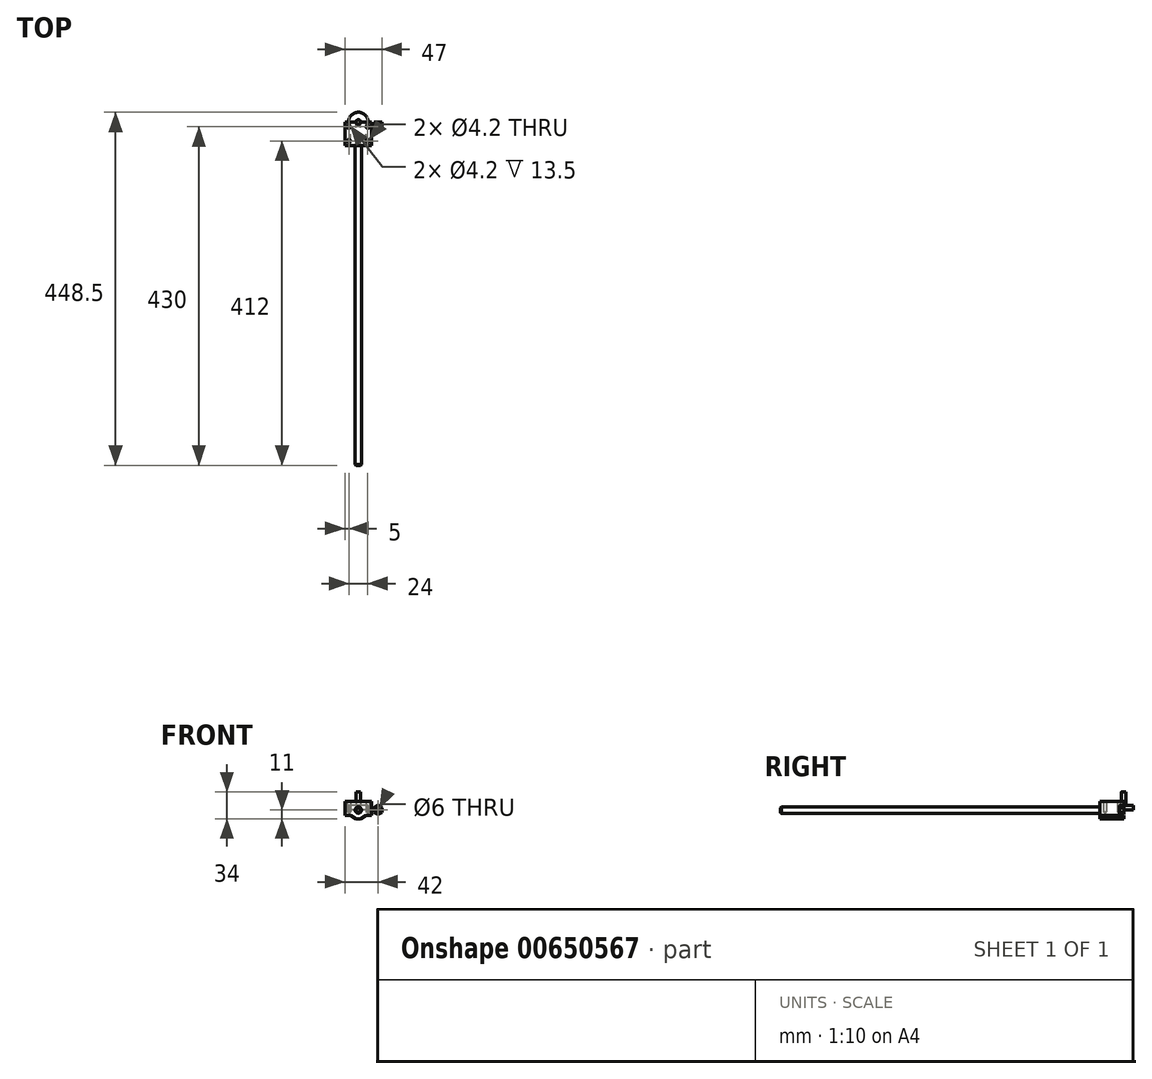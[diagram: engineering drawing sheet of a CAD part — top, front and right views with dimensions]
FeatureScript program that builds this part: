
annotation { "Feature Type Name" : "Feature", "Feature Type Description" : "" }
export const myFeature = defineFeature(function(context is Context, id is Id, definition is map)
    precondition{}
    {
        {
            var Q0;
            Q0=qCreatedBy(makeId("Front.planeOp"),FACE);
            var sketch = newSketch(context, id + "F0", { "sketchPlane" : qUnion([Q0])});
            skCircle(sketch, "E0", {"center": v(0, 0) * mm, "radius": 4 * mm});
            skSolve(sketch);
        }
        {
            var Q0;
            Q0=makeQuery(id+"F0.imprint","IMPRINT",FACE,{"disambiguationData":[TD([[makeQuery(id+"F0.imprint","IMPRINT",EDGE,{"derivedFrom":sQuery(id+"F0.wireOp",EDGE,"E0")}),1.0]])]});
            extrude(context, id + "F1", {"entities" : qUnion([Q0]), "depth" : 380 * mm, "offsetDistance" : 25 * mm});
        }
        {
            var Q0;
            Q0=makeQuery(id+"F0.imprint","IMPRINT",FACE,{"disambiguationData":[TD([[makeQuery(id+"F0.imprint","IMPRINT",EDGE,{"derivedFrom":sQuery(id+"F0.wireOp",EDGE,"E0")}),1.0]])]});
            extrude(context, id + "F2", {"entities" : qUnion([Q0]), "depth" : 436 * mm, "offsetDistance" : 25 * mm});
        }
        {
            var Q0;
            Q0=makeQuery(id+"F1.opExtrude","CAP_EDGE",EDGE,{"disambiguationData":[OSD([sQuery(id+"F0.wireOp",EDGE,"E0")])],"isStart":false});
            var Q1;
            Q1=makeQuery(id+"F1.opExtrude","CAP_EDGE",EDGE,{"disambiguationData":[OSD([sQuery(id+"F0.wireOp",EDGE,"E0")])],"isStart":true});
            var Q2;
            Q2=makeQuery(id+"F2.opExtrude","CAP_EDGE",EDGE,{"disambiguationData":[OSD([sQuery(id+"F0.wireOp",EDGE,"E0")])],"isStart":false});
            var Q3;
            Q3=makeQuery(id+"F2.opExtrude","CAP_EDGE",EDGE,{"disambiguationData":[OSD([sQuery(id+"F0.wireOp",EDGE,"E0")])],"isStart":true});
            chamfer(context, id + "F3", {"entities" : qUnion([Q0, Q1, Q2, Q3]), "width" : 1 * mm, "tangentPropagation" : true});
        }
        {
            var Q0;
            Q0=qCreatedBy(makeId("Front.planeOp"),FACE);
            var sketch = newSketch(context, id + "F4", { "sketchPlane" : qUnion([Q0])});
            skCircle(sketch, "E1.cCircle", {"center": v(0, 0) * mm, "radius": 6.5 * mm, "construction": true});
            skLineSegment(sketch, "E1.0", {"start": v(6.5, 3.75) * mm, "end": v(6.5, -3.75) * mm});
            skLineSegment(sketch, "E1.1", {"start": v(6.5, -3.75) * mm, "end": v(0, -7.5) * mm});
            skLineSegment(sketch, "E1.2", {"start": v(0, -7.5) * mm, "end": v(-6.5, -3.75) * mm});
            skLineSegment(sketch, "E1.3", {"start": v(-6.5, -3.75) * mm, "end": v(-6.5, 3.75) * mm});
            skLineSegment(sketch, "E1.4", {"start": v(-6.5, 3.75) * mm, "end": v(0, 7.5) * mm});
            skLineSegment(sketch, "E1.5", {"start": v(0, 7.5) * mm, "end": v(6.5, 3.75) * mm});
            skPoint(sketch, "E1.0.midPoint", {"position": v(6.5, 0) * mm});
            skCircle(sketch, "E2", {"center": v(0, 0) * mm, "radius": 4 * mm});
            skCircle(sketch, "E3.cCircle", {"center": v(25, 0) * mm, "radius": 5 * mm, "construction": true});
            skLineSegment(sketch, "E3.0", {"start": v(30, 2.89) * mm, "end": v(30, -2.89) * mm});
            skLineSegment(sketch, "E3.1", {"start": v(30, -2.89) * mm, "end": v(25, -5.77) * mm});
            skLineSegment(sketch, "E3.2", {"start": v(25, -5.77) * mm, "end": v(20, -2.89) * mm});
            skLineSegment(sketch, "E3.3", {"start": v(20, -2.89) * mm, "end": v(20, 2.89) * mm});
            skLineSegment(sketch, "E3.4", {"start": v(20, 2.89) * mm, "end": v(25, 5.77) * mm});
            skLineSegment(sketch, "E3.5", {"start": v(25, 5.77) * mm, "end": v(30, 2.89) * mm});
            skPoint(sketch, "E3.0.midPoint", {"position": v(30, 0) * mm});
            skCircle(sketch, "E4", {"center": v(25, 0) * mm, "radius": 3 * mm});
            skSolve(sketch);
        }
        {
            var Q0;
            Q0=makeQuery(id+"F4.imprint","IMPRINT",FACE,{"disambiguationData":[TD([[makeQuery(id+"F4.imprint","IMPRINT",EDGE,{"derivedFrom":sQuery(id+"F4.wireOp",EDGE,"E1.0")}),-1.0]])]});
            extrude(context, id + "F5", {"entities" : qUnion([Q0]), "depth" : 5 * mm, "offsetDistance" : 25 * mm});
        }
        {
            var Q0;
            Q0=makeQuery(id+"F4.imprint","IMPRINT",FACE,{"disambiguationData":[TD([[makeQuery(id+"F4.imprint","IMPRINT",EDGE,{"derivedFrom":sQuery(id+"F4.wireOp",EDGE,"E3.0")}),-1.0]])]});
            extrude(context, id + "F6", {"entities" : qUnion([Q0]), "depth" : 5.24 * mm, "offsetDistance" : 25 * mm});
        }
        {
            var Q0;
            Q0=qCreatedBy(makeId("Front.planeOp"),FACE);
            var sketch = newSketch(context, id + "F7", { "sketchPlane" : qUnion([Q0])});
            skCircle(sketch, "E5", {"center": v(0, 0) * mm, "radius": 4 * mm});
            skLineSegment(sketch, "E6", {"start": v(-17, -11) * mm, "end": v(-17, 11) * mm});
            skLineSegment(sketch, "E7", {"start": v(17, -11) * mm, "end": v(17, 11) * mm});
            skLineSegment(sketch, "E8", {"start": v(-17, 11) * mm, "end": v(17, 11) * mm});
            skLineSegment(sketch, "E9", {"start": v(-17, -11) * mm, "end": v(17, -11) * mm});
            skLineSegment(sketch, "E10", {"start": v(-17, -7) * mm, "end": v(17, -7) * mm, "construction": true});
            skLineSegment(sketch, "E11", {"start": v(-10, -21.27) * mm, "end": v(-10, 22.63) * mm, "construction": true});
            skLineSegment(sketch, "E12", {"start": v(10, -21.27) * mm, "end": v(10, 22.63) * mm, "construction": true});
            skLineSegment(sketch, "E13", {"start": v(-3, -20.4) * mm, "end": v(-3, 23.5) * mm, "construction": true});
            skLineSegment(sketch, "E14", {"start": v(3, -20.4) * mm, "end": v(3, 23.5) * mm, "construction": true});
            skLineSegment(sketch, "E15", {"start": v(-10, -7) * mm, "end": v(-3, -11) * mm});
            skLineSegment(sketch, "E16", {"start": v(17, -7) * mm, "end": v(10, -7) * mm});
            skLineSegment(sketch, "E17", {"start": v(10, -7) * mm, "end": v(3, -11) * mm});
            skLineSegment(sketch, "E18", {"start": v(-17, -7) * mm, "end": v(-10, -7) * mm});
            skSolve(sketch);
        }
        {
            var Q0;
            Q0=makeQuery(id+"F7.imprint","IMPRINT",FACE,{"disambiguationData":[TD([[makeQuery(id+"F7.imprint","IMPRINT",EDGE,{"derivedFrom":sQuery(id+"F7.wireOp",EDGE,"E5")}),-1.0]])]});
            extrude(context, id + "F8", {"entities" : qUnion([Q0]), "depth" : 30 * mm, "offsetDistance" : 25 * mm});
        }
        {
            var Q0;
            Q0=makeQuery(id+"F8.opExtrude","SWEPT_FACE",FACE,{"disambiguationData":[OSD([sQuery(id+"F7.wireOp",EDGE,"E8")])]});
            var sketch = newSketch(context, id + "F9", { "sketchPlane" : qUnion([Q0])});
            skLineSegment(sketch, "E19", {"start": v(-17, 0) * mm, "end": v(17, 0) * mm, "construction": true});
            skLineSegment(sketch, "E20.0", {"start": v(-17, -6) * mm, "end": v(17, -6) * mm, "construction": true});
            skLineSegment(sketch, "E21.0", {"start": v(-17, -24) * mm, "end": v(17, -24) * mm, "construction": true});
            skLineSegment(sketch, "E22", {"start": v(-12, 0) * mm, "end": v(-12, -30) * mm, "construction": true});
            skLineSegment(sketch, "E23", {"start": v(12, 0) * mm, "end": v(12, -30) * mm, "construction": true});
            skPoint(sketch, "E24", {"position": v(-12, -6) * mm});
            skPoint(sketch, "E25", {"position": v(12, -6) * mm});
            skPoint(sketch, "E26", {"position": v(12, -24) * mm});
            skPoint(sketch, "E27", {"position": v(-12, -24) * mm});
            skSolve(sketch);
        }
        {
            var Q0;
            Q0=sQuery(id+"F9.wireOp",VERTEX,"E26");
            var Q1;
            Q1=sQuery(id+"F9.wireOp",VERTEX,"E25");
            var Q2;
            Q2=sQuery(id+"F9.wireOp",VERTEX,"E24");
            var Q3;
            Q3=sQuery(id+"F9.wireOp",VERTEX,"E27");
            var Q4;
            Q4=makeQuery(id+"F8.opExtrude","SWEPT_BODY",BODY,{"disambiguationData":[OSD([sQuery(id+"F7.wireOp",EDGE,"E5"),sQuery(id+"F7.wireOp",EDGE,"E6"),sQuery(id+"F7.wireOp",EDGE,"E7"),sQuery(id+"F7.wireOp",EDGE,"E8"),sQuery(id+"F7.wireOp",EDGE,"E9"),sQuery(id+"F7.wireOp",EDGE,"E15"),sQuery(id+"F7.wireOp",EDGE,"E16"),sQuery(id+"F7.wireOp",EDGE,"E17"),sQuery(id+"F7.wireOp",EDGE,"E18")])]});
            hole(context, id + "F10", {"style" : HoleStyle.SIMPLE, "endStyle" : HoleEndStyle.BLIND, "standardTappedOrClearance" : lookupTablePath({ "standard" : "ISO", "fit" : "Close", "size" : "M4", "type" : "Clearance" }), "standardBlindInLast" : lookupTablePath({ "fit" : "Close", "standard" : "ISO", "size" : "M4", "type" : "Clearance" }), "holeDiameter" : 4.2 * mm, "majorDiameter" : 4 * mm, "holeDepth" : 13.5 * mm, "isTappedThrough" : true, "tappedDepth" : 12 * mm, "tapClearance" : 3, "locations" : qUnion([Q0, Q1, Q2, Q3]), "scope" : qUnion([Q4])});
        }
        {
            var Q0;
            Q0=qCreatedBy(makeId("Top.planeOp"),FACE);
            var sketch = newSketch(context, id + "F11", { "sketchPlane" : qUnion([Q0])});
            skCircle(sketch, "E28", {"center": v(0, 0) * mm, "radius": 12.5 * mm});
            skCircle(sketch, "E29", {"center": v(0, 0) * mm, "radius": 3 * mm});
            skSolve(sketch);
        }
        {
            var Q0;
            Q0=makeQuery(id+"F11.imprint","IMPRINT",FACE,{"disambiguationData":[TD([[makeQuery(id+"F11.imprint","IMPRINT",EDGE,{"derivedFrom":sQuery(id+"F11.wireOp",EDGE,"E28")}),1.0]])]});
            extrude(context, id + "F12", {"entities" : qUnion([Q0]), "depth" : 6 * mm, "offsetDistance" : 25 * mm});
        }
        {
            var Q0;
            Q0=makeQuery(id+"F11.imprint","IMPRINT",FACE,{"disambiguationData":[TD([[makeQuery(id+"F11.imprint","IMPRINT",EDGE,{"derivedFrom":sQuery(id+"F11.wireOp",EDGE,"E29")}),1.0]])]});
            extrude(context, id + "F13", {"entities" : qUnion([Q0]), "operationType" : NewBodyOperationType.ADD, "depth" : (17 + 6) * mm, "offsetDistance" : 25 * mm});
        }
    });
